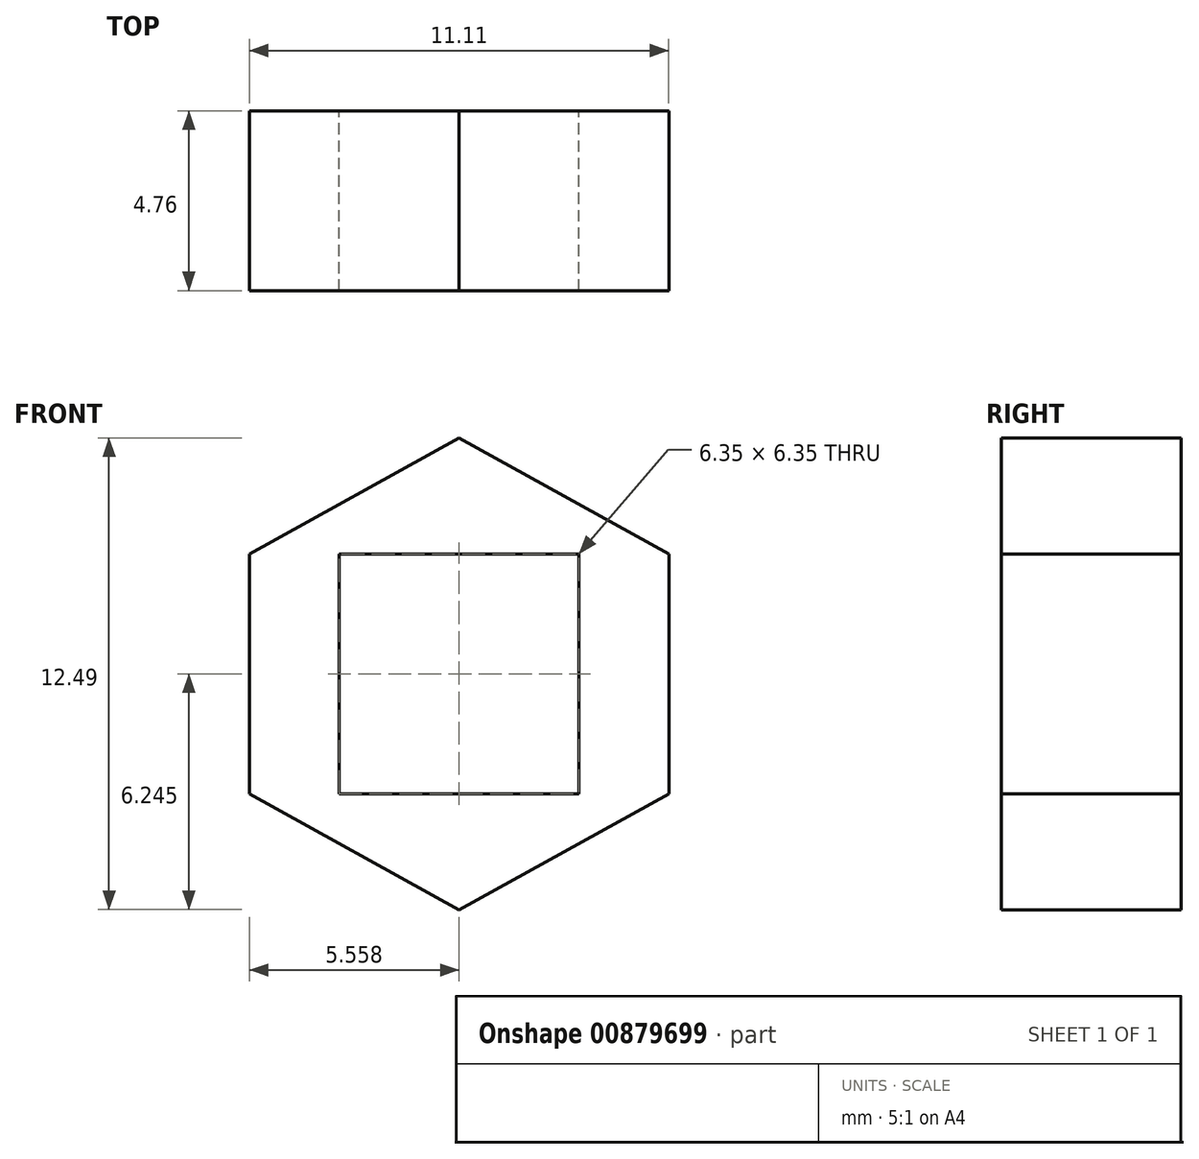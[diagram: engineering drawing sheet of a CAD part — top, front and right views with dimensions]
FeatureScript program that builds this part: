
annotation { "Feature Type Name" : "Feature", "Feature Type Description" : "" }
export const myFeature = defineFeature(function(context is Context, id is Id, definition is map)
    precondition{}
    {
        {
            var Q0;
            Q0=qCreatedBy(makeId("Front.planeOp"),FACE);
            var sketch = newSketch(context, id + "F0", { "sketchPlane" : qUnion([Q0])});
            skLineSegment(sketch, "E0", {"start": v(-38.89, 28.1) * mm, "end": v(-38.89, 21.76) * mm});
            skLineSegment(sketch, "E1", {"start": v(-27.78, 28.1) * mm, "end": v(-27.78, 21.76) * mm});
            skLineSegment(sketch, "E2", {"start": v(-38.89, 28.1) * mm, "end": v(-33.33, 31.18) * mm});
            skLineSegment(sketch, "E3", {"start": v(-33.33, 31.18) * mm, "end": v(-27.78, 28.1) * mm});
            skLineSegment(sketch, "E4", {"start": v(-38.89, 21.76) * mm, "end": v(-33.33, 18.69) * mm});
            skLineSegment(sketch, "E5", {"start": v(-33.33, 18.69) * mm, "end": v(-27.78, 21.76) * mm});
            skLineSegment(sketch, "E6.bottom", {"start": v(-30.16, 21.76) * mm, "end": v(-36.5, 21.76) * mm});
            skLineSegment(sketch, "E6.top", {"start": v(-30.16, 28.1) * mm, "end": v(-36.5, 28.1) * mm});
            skLineSegment(sketch, "E6.left", {"start": v(-30.16, 21.76) * mm, "end": v(-30.16, 28.1) * mm});
            skLineSegment(sketch, "E6.right", {"start": v(-36.5, 21.76) * mm, "end": v(-36.5, 28.1) * mm});
            skSolve(sketch);
        }
        {
            var Q0;
            Q0 = qSketchRegion(id + "F0", true);
            extrude(context, id + "F1", {"entities" : qUnion([Q0]), "depth" : 4.76 * mm, "offsetDistance" : 25.4 * mm});
        }
    });
